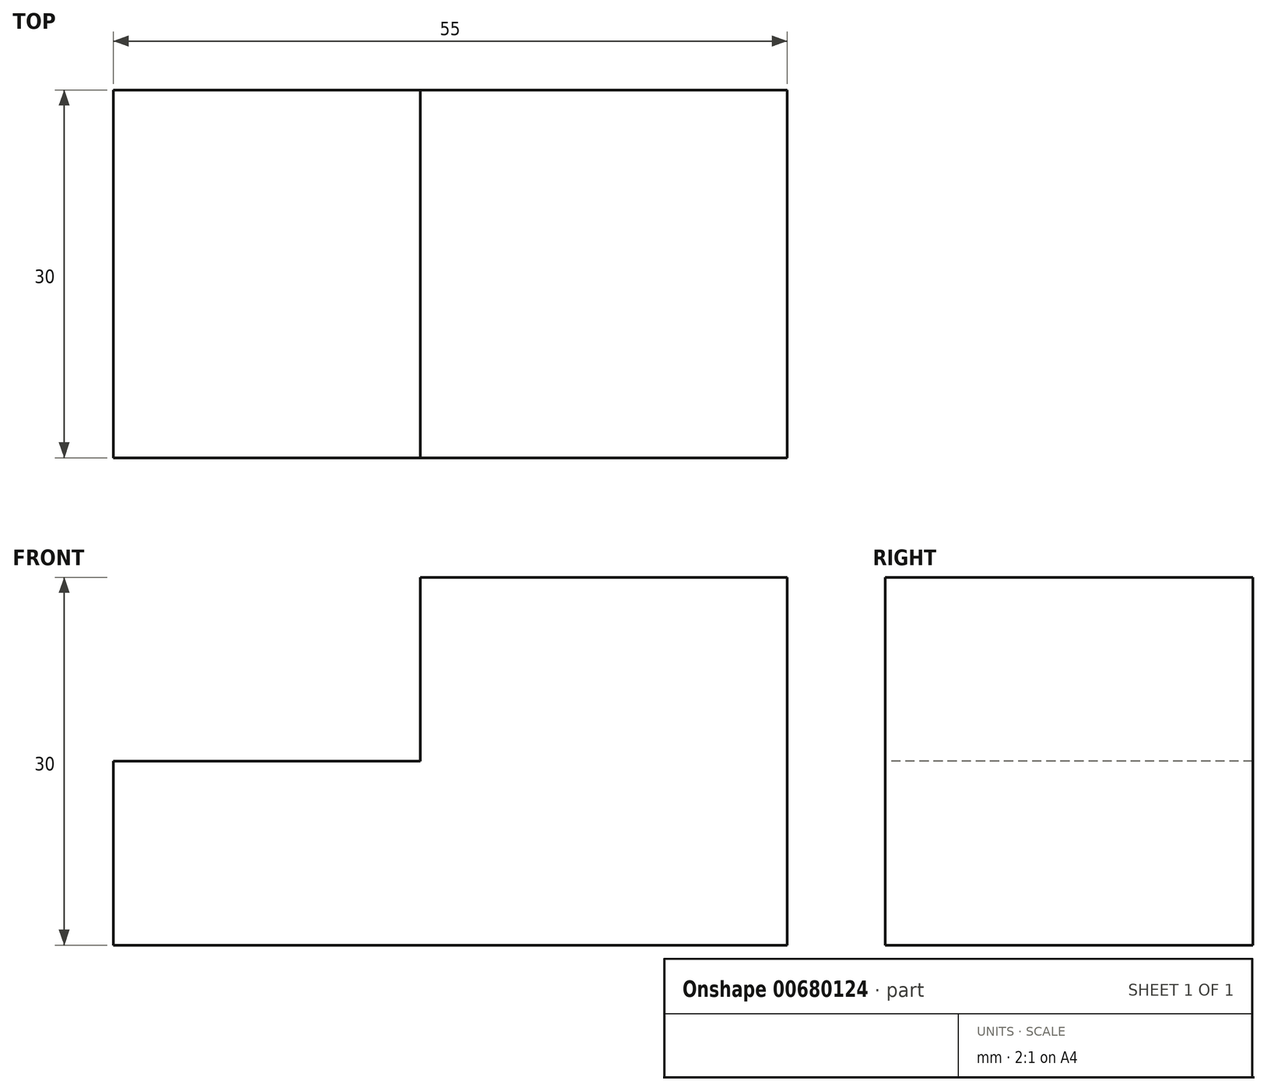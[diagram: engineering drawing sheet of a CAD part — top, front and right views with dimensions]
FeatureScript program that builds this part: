
annotation { "Feature Type Name" : "Feature", "Feature Type Description" : "" }
export const myFeature = defineFeature(function(context is Context, id is Id, definition is map)
    precondition{}
    {
        {
            var Q0;
            Q0=qCreatedBy(makeId("Top.planeOp"),FACE);
            var sketch = newSketch(context, id + "F0", { "sketchPlane" : qUnion([Q0])});
            skLineSegment(sketch, "E0.bottom", {"start": v(-27.5, 15) * mm, "end": v(27.5, 15) * mm});
            skLineSegment(sketch, "E0.top", {"start": v(-27.5, -15) * mm, "end": v(27.5, -15) * mm});
            skLineSegment(sketch, "E0.left", {"start": v(-27.5, 15) * mm, "end": v(-27.5, -15) * mm});
            skLineSegment(sketch, "E0.right", {"start": v(27.5, 15) * mm, "end": v(27.5, -15) * mm});
            skPoint(sketch, "E0.middle", {"position": v(0, 0) * mm});
            skSolve(sketch);
        }
        {
            var Q0;
            Q0=makeQuery(id+"F0.imprint","IMPRINT",FACE,{"disambiguationData":[TD([[makeQuery(id+"F0.imprint","IMPRINT",EDGE,{"derivedFrom":sQuery(id+"F0.wireOp",EDGE,"E0.bottom")}),-1.0]])]});
            extrude(context, id + "F1", {"entities" : qUnion([Q0]), "depth" : 30 * mm, "offsetDistance" : 25 * mm});
        }
        {
            var Q0;
            Q0=makeQuery(id+"F1.opExtrude","SWEPT_FACE",FACE,{"disambiguationData":[OSD([sQuery(id+"F0.wireOp",EDGE,"E0.top")])]});
            var sketch = newSketch(context, id + "F2", { "sketchPlane" : qUnion([Q0])});
            skLineSegment(sketch, "E1", {"start": v(-27.5, 15) * mm, "end": v(-2.45, 15) * mm});
            skLineSegment(sketch, "E2", {"start": v(-2.45, 15) * mm, "end": v(-2.45, 30) * mm});
            skSolve(sketch);
        }
        {
            var Q0;
            Q0 = qSketchRegion(id + "F2", true);
            var Q1;
            {var subQ0=sQuery(id+"F2.wireOp",EDGE,"E1");Q1=makeQuery(id+"F2.imprint","IMPRINT",FACE,{"disambiguationData":[TD([[makeQuery(id+"F2.imprint","IMPRINT",EDGE,{"derivedFrom":subQ0}),1.0]])]});}
            extrude(context, id + "F3", {"entities" : qUnion([Q0, Q1]), "operationType" : NewBodyOperationType.REMOVE, "endBound" : BoundingType.THROUGH_ALL, "oppositeDirection" : true, "depth" : 25 * mm, "offsetDistance" : 25 * mm});
        }
    });
